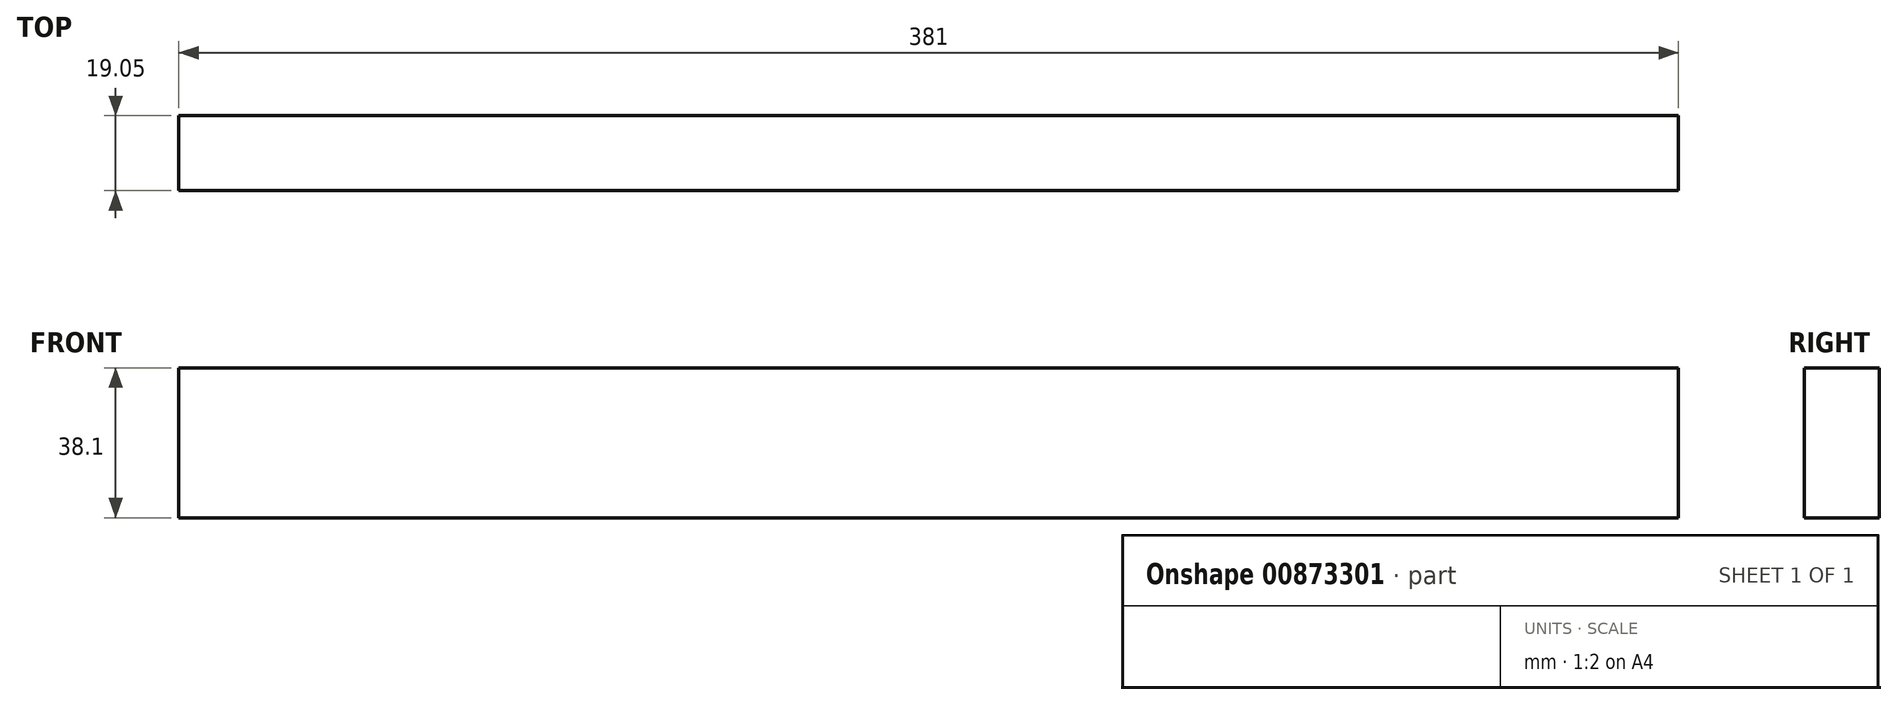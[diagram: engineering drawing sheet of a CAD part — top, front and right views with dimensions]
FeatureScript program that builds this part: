
annotation { "Feature Type Name" : "Feature", "Feature Type Description" : "" }
export const myFeature = defineFeature(function(context is Context, id is Id, definition is map)
    precondition{}
    {
        {
            var Q0;
            Q0=qCreatedBy(makeId("Front.planeOp"),FACE);
            var sketch = newSketch(context, id + "F0", { "sketchPlane" : qUnion([Q0])});
            skLineSegment(sketch, "E0.bottom", {"start": v(0, 0) * mm, "end": v(-381, 0) * mm});
            skLineSegment(sketch, "E0.top", {"start": v(0, 38.1) * mm, "end": v(-381, 38.1) * mm});
            skLineSegment(sketch, "E0.left", {"start": v(0, 0) * mm, "end": v(0, 38.1) * mm});
            skLineSegment(sketch, "E0.right", {"start": v(-381, 0) * mm, "end": v(-381, 38.1) * mm});
            skSolve(sketch);
        }
        {
            var Q0;
            Q0=makeQuery(id+"F0.imprint","IMPRINT",FACE,{"disambiguationData":[TD([[makeQuery(id+"F0.imprint","IMPRINT",EDGE,{"derivedFrom":sQuery(id+"F0.wireOp",EDGE,"E0.bottom")}),-1.0]])]});
            extrude(context, id + "F1", {"entities" : qUnion([Q0]), "depth" : 19.05 * mm, "offsetDistance" : 25.4 * mm});
        }
    });
